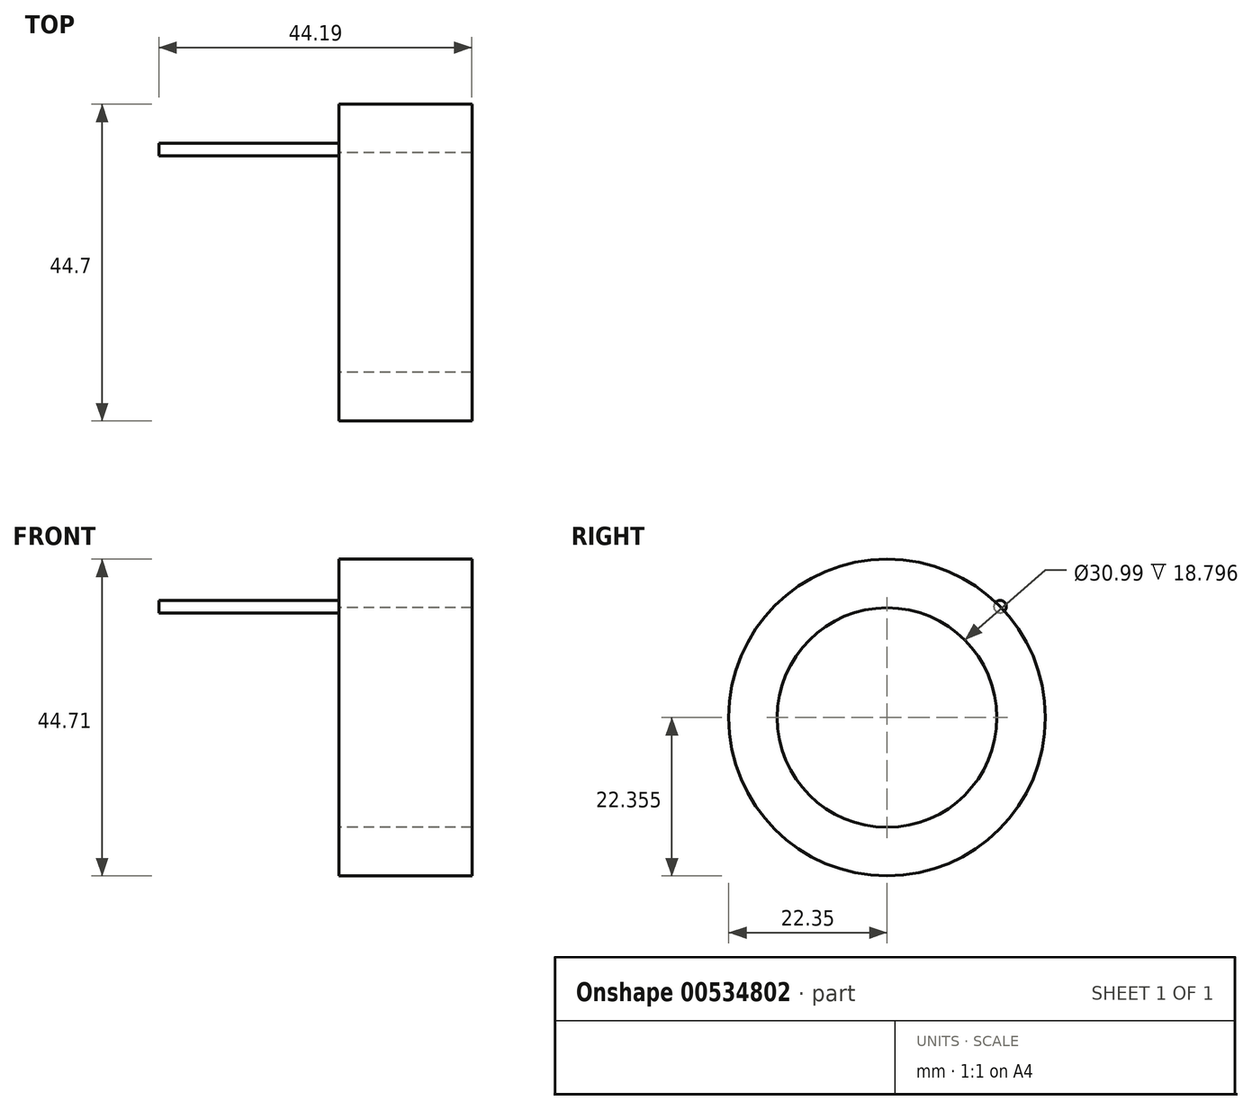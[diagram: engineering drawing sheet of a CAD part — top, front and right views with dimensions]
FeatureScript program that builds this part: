
annotation { "Feature Type Name" : "Feature", "Feature Type Description" : "" }
export const myFeature = defineFeature(function(context is Context, id is Id, definition is map)
    precondition{}
    {
        {
            var Q0;
            Q0=qCreatedBy(makeId("Front.planeOp"),FACE);
            var sketch = newSketch(context, id + "F0", { "sketchPlane" : qUnion([Q0])});
            skLineSegment(sketch, "E0", {"start": v(-48, 36.83) * mm, "end": v(-23.37, 36.83) * mm});
            skLineSegment(sketch, "E1", {"start": v(-42.16, 36.83) * mm, "end": v(-42.16, 29.97) * mm});
            skLineSegment(sketch, "E2", {"start": v(-42.16, 29.97) * mm, "end": v(-23.37, 29.97) * mm});
            skLineSegment(sketch, "E3", {"start": v(-23.37, 29.97) * mm, "end": v(-23.37, 36.83) * mm});
            skLineSegment(sketch, "E4", {"start": v(-50.55, 14.48) * mm, "end": v(-17.78, 14.48) * mm});
            skSolve(sketch);
        }
        {
            var Q0;
            Q0 = qSketchRegion(id + "F0", true);
            var Q1;
            Q1=sQuery(id+"F0.wireOp",EDGE,"E4");
            revolve(context, id + "F1", {"entities" : qUnion([Q0]), "axis" : qUnion([Q1]), "revolveType" : RevolveType.FULL});
        }
        {
            var Q0;
            Q0=makeQuery(id+"F1.opRevolve","SWEPT_FACE",FACE,{"disambiguationData":[OSD([sQuery(id+"F0.wireOp",EDGE,"E1")])]});
            var sketch = newSketch(context, id + "F2", { "sketchPlane" : qUnion([Q0])});
            skCircle(sketch, "E5", {"center": v(-15.95, 30.13) * mm, "radius": 0.88 * mm});
            skSolve(sketch);
        }
        {
            var Q0;
            Q0 = qSketchRegion(id + "F2", true);
            extrude(context, id + "F3", {"entities" : qUnion([Q0]), "operationType" : NewBodyOperationType.ADD, "depth" : 25.4 * mm, "offsetDistance" : 25.4 * mm});
        }
    });
